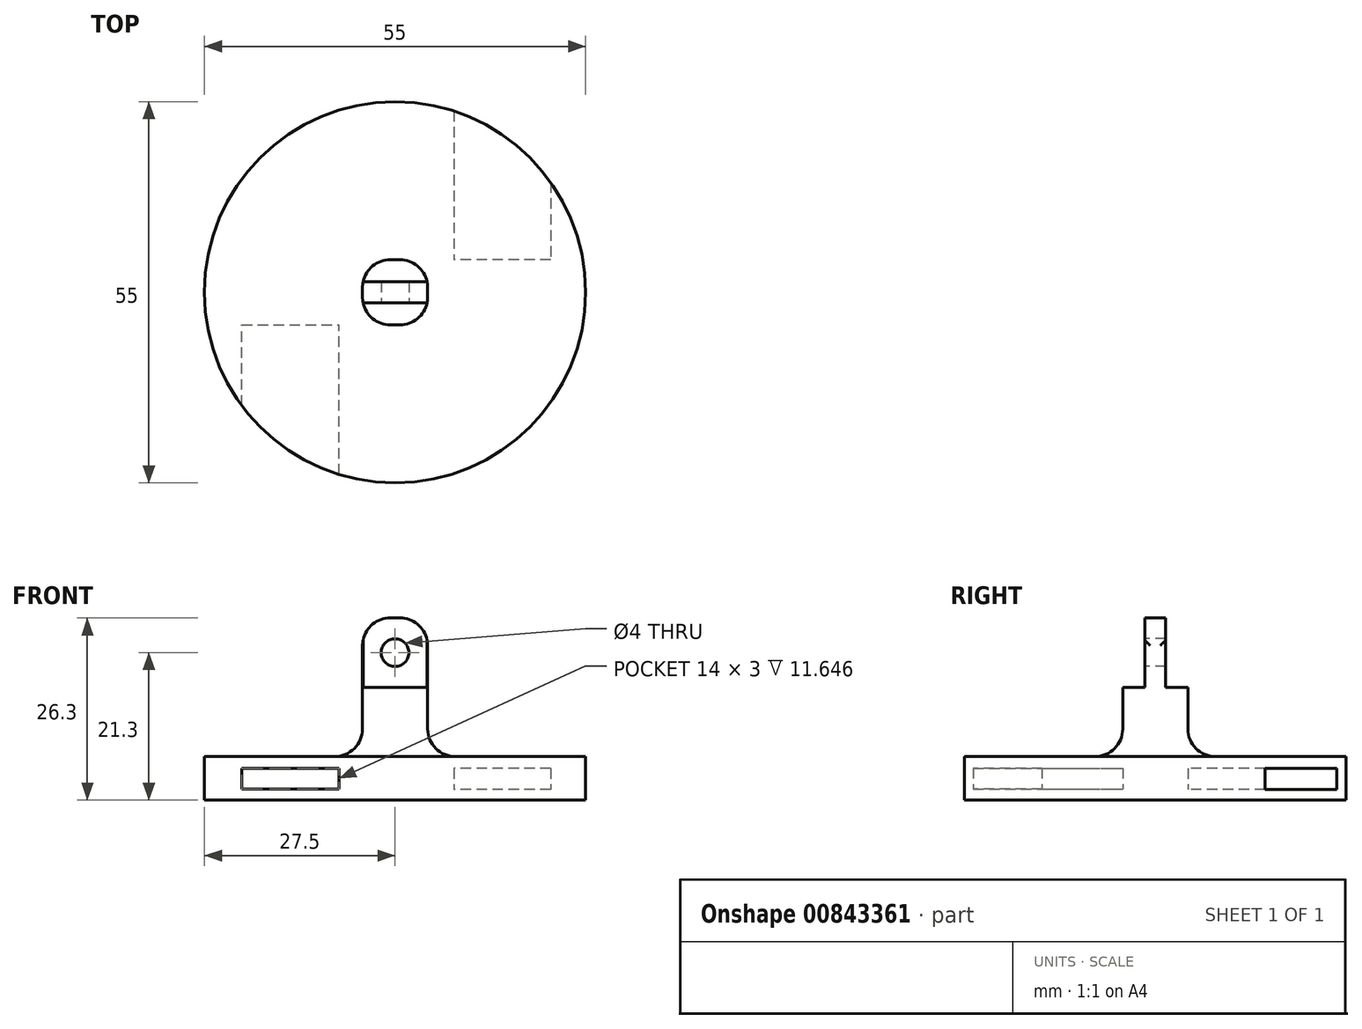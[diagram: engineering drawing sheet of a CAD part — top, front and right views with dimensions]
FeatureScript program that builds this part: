
annotation { "Feature Type Name" : "Feature", "Feature Type Description" : "" }
export const myFeature = defineFeature(function(context is Context, id is Id, definition is map)
    precondition{}
    {
        {
            var Q0;
            Q0=qCreatedBy(makeId("Top.planeOp"),FACE);
            cPlane(context, id + "F0", {"entities" : qUnion([Q0]), "cplaneType" : CPlaneType.OFFSET, "offset" : 3.6 * mm, "width" : 150 * mm, "height" : 150 * mm});
        }
        {
            var Q0;
            Q0=qCreatedBy(id+"F0.planeOp",FACE);
            var sketch = newSketch(context, id + "F1", { "sketchPlane" : qUnion([Q0])});
            skCircle(sketch, "E0", {"center": v(0, 0) * mm, "radius": 27.5 * mm});
            skSolve(sketch);
        }
        {
            var Q0;
            Q0 = qSketchRegion(id + "F1", true);
            extrude(context, id + "F2", {"entities" : qUnion([Q0]), "depth" : 6.3 * mm, "offsetDistance" : 25 * mm});
        }
        {
            var Q0;
            Q0=makeQuery(id+"F2.opExtrude","CAP_FACE",FACE,{"disambiguationData":[OSD([sQuery(id+"F1.wireOp",EDGE,"E0")])],"isStart":false});
            var sketch = newSketch(context, id + "F3", { "sketchPlane" : qUnion([Q0])});
            skLineSegment(sketch, "E1.bottom", {"start": v(4.7, -4.7) * mm, "end": v(-4.7, -4.7) * mm});
            skLineSegment(sketch, "E1.top", {"start": v(4.7, 4.7) * mm, "end": v(-4.7, 4.7) * mm});
            skLineSegment(sketch, "E1.left", {"start": v(4.7, -4.7) * mm, "end": v(4.7, 4.7) * mm});
            skLineSegment(sketch, "E1.right", {"start": v(-4.7, -4.7) * mm, "end": v(-4.7, 4.7) * mm});
            skPoint(sketch, "E1.middle", {"position": v(0, 0) * mm});
            skSolve(sketch);
        }
        {
            var Q0;
            Q0 = qSketchRegion(id + "F3", true);
            extrude(context, id + "F4", {"entities" : qUnion([Q0]), "operationType" : NewBodyOperationType.ADD, "depth" : 10 * mm, "offsetDistance" : 25 * mm});
        }
        {
            var Q0;
            Q0=makeQuery(id+"F4.opExtrude","CAP_FACE",FACE,{"disambiguationData":[OSD([sQuery(id+"F3.wireOp",EDGE,"E1.bottom"),sQuery(id+"F3.wireOp",EDGE,"E1.top"),sQuery(id+"F3.wireOp",EDGE,"E1.left"),sQuery(id+"F3.wireOp",EDGE,"E1.right")])],"isStart":false});
            var sketch = newSketch(context, id + "F5", { "sketchPlane" : qUnion([Q0])});
            skLineSegment(sketch, "E2.bottom", {"start": v(-4.7, 1.5) * mm, "end": v(4.7, 1.5) * mm});
            skLineSegment(sketch, "E2.top", {"start": v(-4.7, -1.5) * mm, "end": v(4.7, -1.5) * mm});
            skLineSegment(sketch, "E2.left", {"start": v(-4.7, 1.5) * mm, "end": v(-4.7, -1.5) * mm});
            skLineSegment(sketch, "E2.right", {"start": v(4.7, 1.5) * mm, "end": v(4.7, -1.5) * mm});
            skSolve(sketch);
        }
        {
            var Q0;
            Q0 = qSketchRegion(id + "F5", true);
            extrude(context, id + "F6", {"entities" : qUnion([Q0]), "operationType" : NewBodyOperationType.ADD, "depth" : 10 * mm, "offsetDistance" : 25 * mm});
        }
        {
            var Q0;
            Q0=makeQuery(id+"F6.opExtrude","SWEPT_FACE",FACE,{"disambiguationData":[OSD([sQuery(id+"F5.wireOp",EDGE,"E2.top")])]});
            var sketch = newSketch(context, id + "F7", { "sketchPlane" : qUnion([Q0])});
            skLineSegment(sketch, "E3", {"start": v(-4.7, 29.9) * mm, "end": v(4.7, 19.9) * mm, "construction": true});
            skCircle(sketch, "E4", {"center": v(0, 24.9) * mm, "radius": 2 * mm});
            skSolve(sketch);
        }
        {
            var Q0;
            Q0=makeQuery(id+"F7.imprint","IMPRINT",FACE,{"disambiguationData":[TD([[makeQuery(id+"F7.imprint","IMPRINT",EDGE,{"derivedFrom":sQuery(id+"F7.wireOp",EDGE,"E4")}),1.0]])]});
            extrude(context, id + "F8", {"entities" : qUnion([Q0]), "operationType" : NewBodyOperationType.REMOVE, "oppositeDirection" : true, "depth" : 25 * mm, "offsetDistance" : 25 * mm});
        }
        {
            var Q0;
            Q0=makeQuery(id+"F6.opExtrude","CAP_EDGE",EDGE,{"disambiguationData":[OSD([sQuery(id+"F5.wireOp",EDGE,"E2.left")])],"isStart":false});
            var Q1;
            Q1=makeQuery(id+"F6.opExtrude","CAP_EDGE",EDGE,{"disambiguationData":[OSD([sQuery(id+"F5.wireOp",EDGE,"E2.right")])],"isStart":false});
            fillet(context, id + "F9", {"entities" : qUnion([Q0, Q1]), "radius" : 4 * mm, "tangentPropagation" : true, "allowEdgeOverflow" : false});
        }
        {
            var Q0;
            Q0=makeQuery(id+"F4.opExtrude","SWEPT_EDGE",EDGE,{"disambiguationData":[OSD([sQuery(id+"F3.wireOp",EDGE,"E1.bottom"),sQuery(id+"F3.wireOp",EDGE,"E1.right")])]});
            var Q1;
            Q1=makeQuery(id+"F4.opExtrude","SWEPT_EDGE",EDGE,{"disambiguationData":[OSD([sQuery(id+"F3.wireOp",EDGE,"E1.top"),sQuery(id+"F3.wireOp",EDGE,"E1.right")])]});
            var Q2;
            Q2=makeQuery(id+"F4.opExtrude","SWEPT_EDGE",EDGE,{"disambiguationData":[OSD([sQuery(id+"F3.wireOp",EDGE,"E1.bottom"),sQuery(id+"F3.wireOp",EDGE,"E1.left")])]});
            var Q3;
            Q3=makeQuery(id+"F4.opExtrude","SWEPT_EDGE",EDGE,{"disambiguationData":[OSD([sQuery(id+"F3.wireOp",EDGE,"E1.top"),sQuery(id+"F3.wireOp",EDGE,"E1.left")])]});
            fillet(context, id + "F10", {"entities" : qUnion([Q0, Q1, Q2, Q3]), "radius" : 4 * mm, "tangentPropagation" : true, "allowEdgeOverflow" : false});
        }
        {
            var Q0;
            Q0=makeQuery(id+"F10.opFillet","BLEND_EDGE",EDGE,{"blendedFrom":[makeQuery(id+"F4.opExtrude","SWEPT_EDGE",EDGE,{"disambiguationData":[OSD([sQuery(id+"F3.wireOp",EDGE,"E1.bottom"),sQuery(id+"F3.wireOp",EDGE,"E1.right")])]}),makeQuery(id+"F2.opExtrude","CAP_FACE",FACE,{"disambiguationData":[OSD([sQuery(id+"F1.wireOp",EDGE,"E0")])],"isStart":false})],"blendedInto":[makeQuery(id+"F2.opExtrude","CAP_FACE",FACE,{"disambiguationData":[OSD([sQuery(id+"F1.wireOp",EDGE,"E0")])],"isStart":false})]});
            fillet(context, id + "F11", {"entities" : qUnion([Q0]), "radius" : 4 * mm, "tangentPropagation" : true, "allowEdgeOverflow" : false});
        }
        {
            var Q0;
            Q0=makeQuery(id+"F4.opExtrude","SWEPT_FACE",FACE,{"disambiguationData":[OSD([sQuery(id+"F3.wireOp",EDGE,"E1.top")])]});
            var sketch = newSketch(context, id + "F12", { "sketchPlane" : qUnion([Q0])});
            skLineSegment(sketch, "E5.bottom", {"start": v(-22.46, 8.18) * mm, "end": v(-8.46, 8.18) * mm});
            skLineSegment(sketch, "E5.top", {"start": v(-22.46, 5.18) * mm, "end": v(-8.46, 5.18) * mm});
            skLineSegment(sketch, "E5.left", {"start": v(-22.46, 8.18) * mm, "end": v(-22.46, 5.18) * mm});
            skLineSegment(sketch, "E5.right", {"start": v(-8.46, 8.18) * mm, "end": v(-8.46, 5.18) * mm});
            skSolve(sketch);
        }
        {
            var Q0;
            Q0 = qSketchRegion(id + "F12", true);
            extrude(context, id + "F13", {"entities" : qUnion([Q0]), "operationType" : NewBodyOperationType.REMOVE, "depth" : 25 * mm, "offsetDistance" : 25 * mm});
        }
        {
            var Q0;
            Q0=makeQuery(id+"F4.opExtrude","SWEPT_FACE",FACE,{"disambiguationData":[OSD([sQuery(id+"F3.wireOp",EDGE,"E1.bottom")])]});
            var sketch = newSketch(context, id + "F14", { "sketchPlane" : qUnion([Q0])});
            skLineSegment(sketch, "E6.bottom", {"start": v(-22.11, 8.2) * mm, "end": v(-8.11, 8.2) * mm});
            skLineSegment(sketch, "E6.top", {"start": v(-22.11, 5.2) * mm, "end": v(-8.11, 5.2) * mm});
            skLineSegment(sketch, "E6.left", {"start": v(-22.11, 8.2) * mm, "end": v(-22.11, 5.2) * mm});
            skLineSegment(sketch, "E6.right", {"start": v(-8.11, 8.2) * mm, "end": v(-8.11, 5.2) * mm});
            skSolve(sketch);
        }
        {
            var Q0;
            Q0 = qSketchRegion(id + "F14", true);
            extrude(context, id + "F15", {"entities" : qUnion([Q0]), "operationType" : NewBodyOperationType.REMOVE, "depth" : 25 * mm, "offsetDistance" : 25 * mm});
        }
    });
